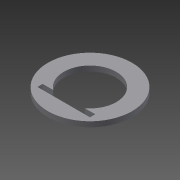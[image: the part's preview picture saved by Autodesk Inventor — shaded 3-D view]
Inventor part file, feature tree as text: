
AUTODESK INVENTOR PART (.ipt)
format: ipt  version: 2014 SP1 (Build 180222100, 222)  size: 83,456 bytes
history: native  units: mm
features: extrude x1, sketch x1
ambient origin geometry x8: Origin, YZ Plane, XZ Plane, XY Plane, X Axis, Y Axis, Z Axis, Center Point
bodies: Solid1 (feature_tree)
feature tree (2):
  extrude  "Extrusion1"  Depth=50.0mm
  sketch  "Sketch1"  dims[d0=80.0mm d1=50.0mm d2=25.0mm d3=5.0mm d4=50.0mm d5=5.0mm d6=0.0mm]
